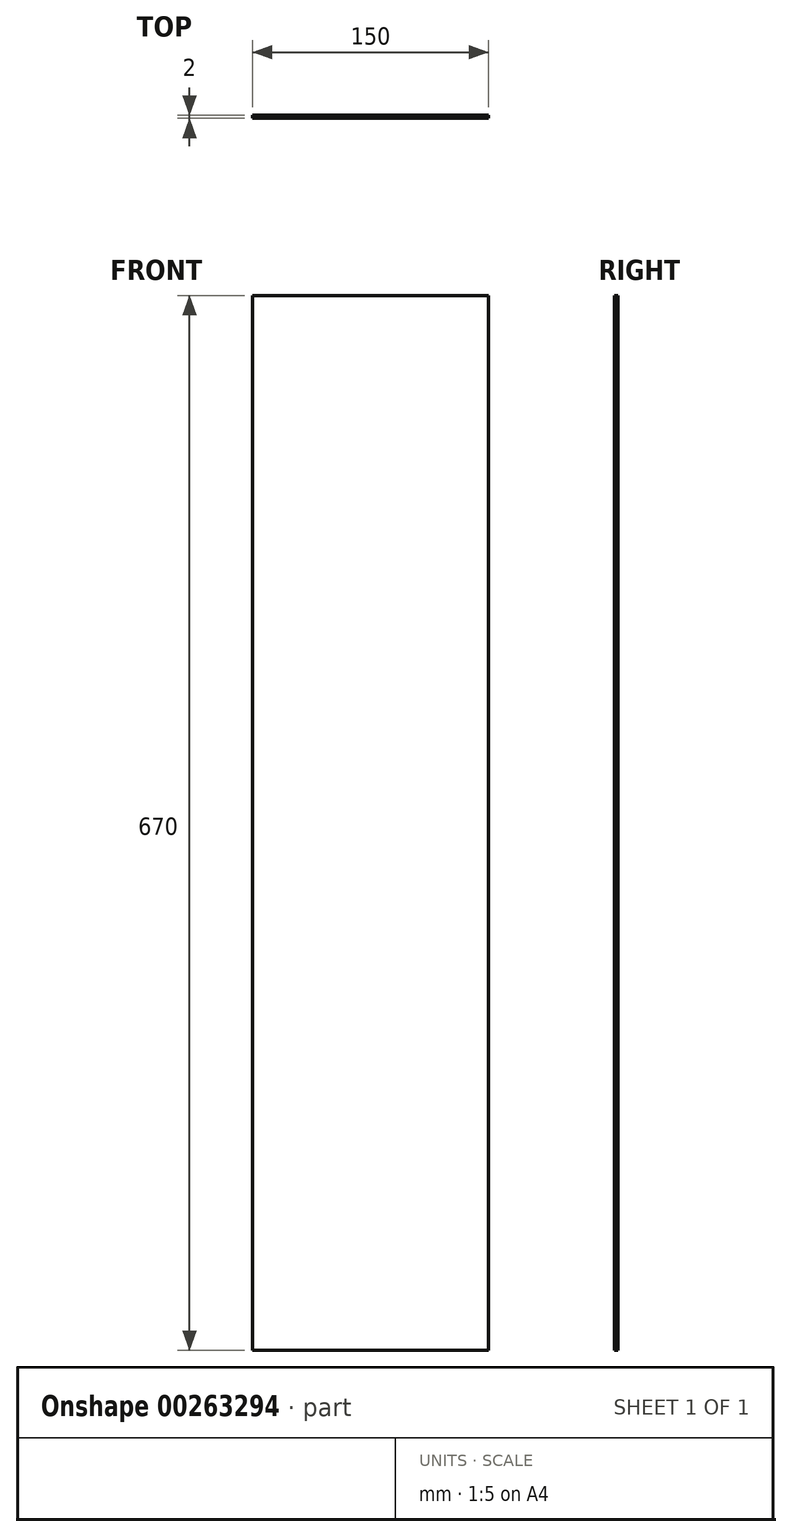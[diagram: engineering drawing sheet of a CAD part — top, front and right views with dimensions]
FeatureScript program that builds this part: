
annotation { "Feature Type Name" : "Feature", "Feature Type Description" : "" }
export const myFeature = defineFeature(function(context is Context, id is Id, definition is map)
    precondition{}
    {
        {
            var Q0;
            Q0=qCreatedBy(makeId("Front.planeOp"),FACE);
            var sketch = newSketch(context, id + "F0", { "sketchPlane" : qUnion([Q0])});
            skLineSegment(sketch, "E0.bottom", {"start": v(75, -335) * mm, "end": v(-75, -335) * mm});
            skLineSegment(sketch, "E0.top", {"start": v(75, 335) * mm, "end": v(-75, 335) * mm});
            skLineSegment(sketch, "E0.left", {"start": v(75, -335) * mm, "end": v(75, 335) * mm});
            skLineSegment(sketch, "E0.right", {"start": v(-75, -335) * mm, "end": v(-75, 335) * mm});
            skPoint(sketch, "E0.middle", {"position": v(0, 0) * mm});
            skSolve(sketch);
        }
        {
            var Q0;
            Q0 = qSketchRegion(id + "F0", true);
            extrude(context, id + "F1", {"entities" : qUnion([Q0]), "depth" : 2 * mm});
        }
    });
